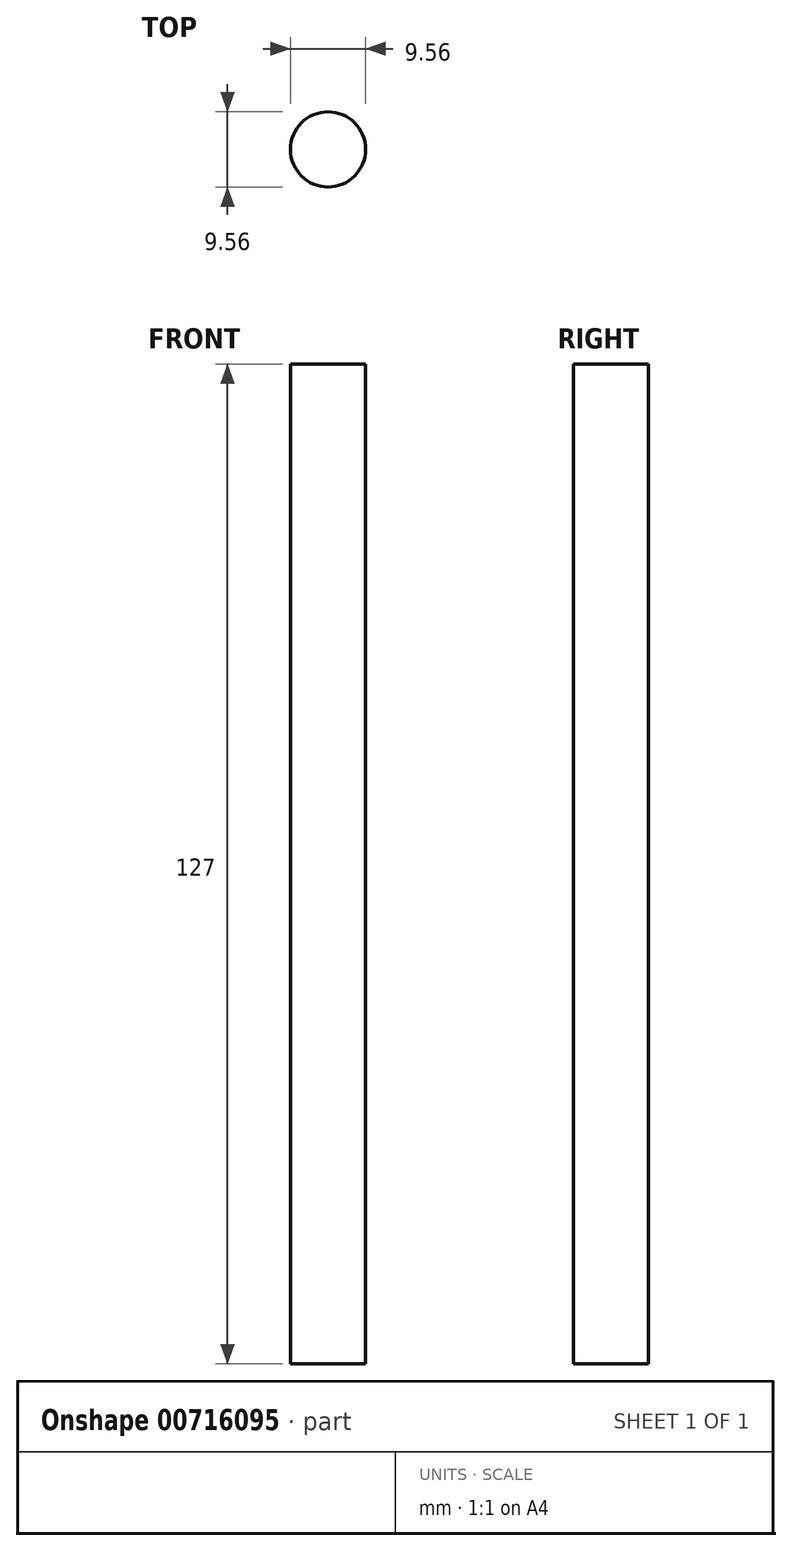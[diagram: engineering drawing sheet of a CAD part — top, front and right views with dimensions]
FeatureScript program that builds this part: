
annotation { "Feature Type Name" : "Feature", "Feature Type Description" : "" }
export const myFeature = defineFeature(function(context is Context, id is Id, definition is map)
    precondition{}
    {
        {
            var Q0;
            Q0=qCreatedBy(makeId("Top.planeOp"),FACE);
            var sketch = newSketch(context, id + "F0", { "sketchPlane" : qUnion([Q0])});
            skCircle(sketch, "E0", {"center": v(0, 0) * mm, "radius": 4.78 * mm});
            skSolve(sketch);
        }
        {
            var Q0;
            Q0 = qSketchRegion(id + "F0", true);
            extrude(context, id + "F1", {"entities" : qUnion([Q0]), "depth" : 127 * mm, "offsetDistance" : 25 * mm});
        }
    });
